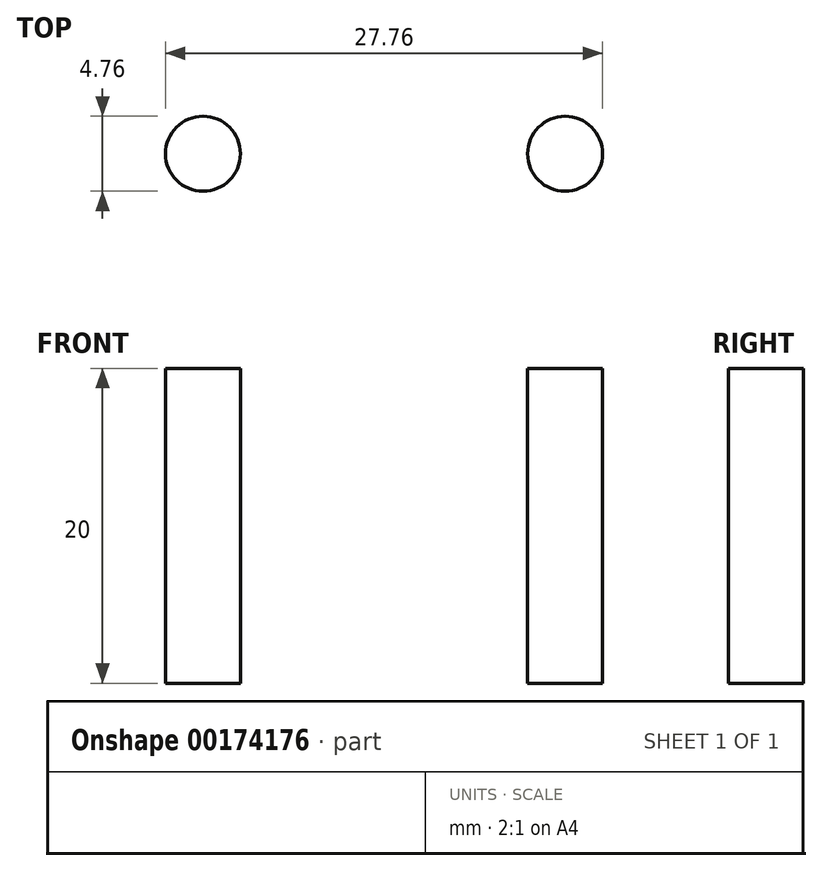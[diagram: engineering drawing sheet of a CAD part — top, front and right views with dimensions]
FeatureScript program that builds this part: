
annotation { "Feature Type Name" : "Feature", "Feature Type Description" : "" }
export const myFeature = defineFeature(function(context is Context, id is Id, definition is map)
    precondition{}
    {
        {
            var Q0;
            Q0=qCreatedBy(makeId("Top.planeOp"),FACE);
            var sketch = newSketch(context, id + "F0", { "sketchPlane" : qUnion([Q0])});
            skLineSegment(sketch, "E0", {"start": v(0, 0) * mm, "end": v(11.5, 0) * mm, "construction": true});
            skLineSegment(sketch, "E1", {"start": v(0, 0) * mm, "end": v(-11.5, 0) * mm, "construction": true});
            skCircle(sketch, "E2", {"center": v(-11.5, 0) * mm, "radius": 2.38 * mm});
            skCircle(sketch, "E3", {"center": v(11.5, 0) * mm, "radius": 2.38 * mm});
            skLineSegment(sketch, "E4", {"start": v(11.5, 0) * mm, "end": v(11.5, 8) * mm, "construction": true});
            skLineSegment(sketch, "E5", {"start": v(-11.5, 0) * mm, "end": v(-11.5, 8) * mm, "construction": true});
            skLineSegment(sketch, "E6", {"start": v(-11.5, 8) * mm, "end": v(-13, 8) * mm, "construction": true});
            skLineSegment(sketch, "E7", {"start": v(11.5, 8) * mm, "end": v(13, 8) * mm, "construction": true});
            skLineSegment(sketch, "E8", {"start": v(-15, 6) * mm, "end": v(-15, 3.24) * mm, "construction": true});
            skLineSegment(sketch, "E9", {"start": v(15, 6) * mm, "end": v(15, 4.48) * mm, "construction": true});
            skLineSegment(sketch, "E10", {"start": v(-60.48, 10.8) * mm, "end": v(-60.48, 35.87) * mm, "construction": true});
            skLineSegment(sketch, "E11", {"start": v(-60.48, 35.87) * mm, "end": v(-20.23, 35.87) * mm, "construction": true});
            skPoint(sketch, "E12.visualSharp", {"position": v(-15, 8) * mm});
            skArc(sketch, "E12.filletArc", {"start": v(-13, 8) * mm, "mid": v(-14.41, 7.41) * mm, "end": v(-15, 6) * mm, "construction": true});
            skPoint(sketch, "E13.visualSharp", {"position": v(15, 8) * mm});
            skArc(sketch, "E13.filletArc", {"start": v(15, 6) * mm, "mid": v(14.41, 7.41) * mm, "end": v(13, 8) * mm, "construction": true});
            skLineSegment(sketch, "E14", {"start": v(0, 5.2) * mm, "end": v(-9.5, 5.2) * mm, "construction": true});
            skLineSegment(sketch, "E15", {"start": v(0, 5.2) * mm, "end": v(9.5, 5.2) * mm, "construction": true});
            skLineSegment(sketch, "E16", {"start": v(0, 17.88) * mm, "end": v(0, 2.38) * mm, "construction": true});
            skLineSegment(sketch, "E17", {"start": v(11.5, 2.38) * mm, "end": v(-11.5, 2.38) * mm, "construction": true});
            skSolve(sketch);
        }
        {
            var Q0;
            Q0 = qSketchRegion(id + "F0", true);
            extrude(context, id + "F1", {"entities" : qUnion([Q0]), "depth" : 20 * mm, "offsetDistance" : 25 * mm});
        }
    });
